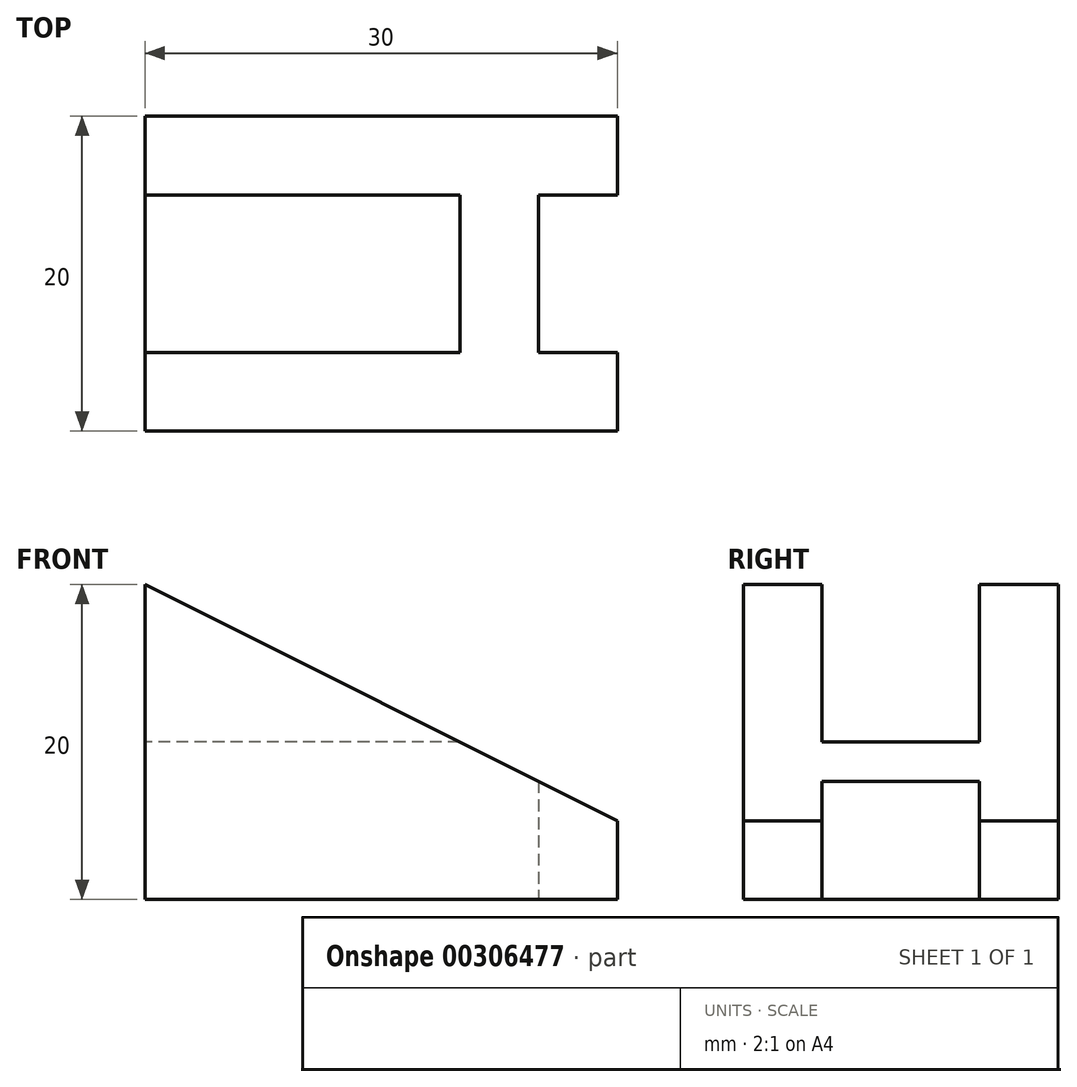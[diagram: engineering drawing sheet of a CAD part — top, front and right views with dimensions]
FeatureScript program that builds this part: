
annotation { "Feature Type Name" : "Feature", "Feature Type Description" : "" }
export const myFeature = defineFeature(function(context is Context, id is Id, definition is map)
    precondition{}
    {
        {
            var Q0;
            Q0=qCreatedBy(makeId("Front.planeOp"),FACE);
            var sketch = newSketch(context, id + "F0", { "sketchPlane" : qUnion([Q0])});
            skLineSegment(sketch, "E0", {"start": v(0, 0) * mm, "end": v(30, 0) * mm});
            skLineSegment(sketch, "E1", {"start": v(30, 0) * mm, "end": v(30, 5) * mm});
            skLineSegment(sketch, "E2", {"start": v(30, 5) * mm, "end": v(0, 20) * mm});
            skLineSegment(sketch, "E3", {"start": v(0, 20) * mm, "end": v(0, 0) * mm});
            skSolve(sketch);
        }
        {
            var Q0;
            Q0=makeQuery(id+"F0.imprint","IMPRINT",FACE,{"disambiguationData":[TD([[makeQuery(id+"F0.imprint","IMPRINT",EDGE,{"derivedFrom":sQuery(id+"F0.wireOp",EDGE,"E0")}),1.0]])]});
            extrude(context, id + "F1", {"entities" : qUnion([Q0]), "depth" : 20 * mm});
        }
        {
            var Q0;
            Q0=makeQuery(id+"F1.opExtrude","SWEPT_FACE",FACE,{"disambiguationData":[OSD([sQuery(id+"F0.wireOp",EDGE,"E0")])]});
            var sketch = newSketch(context, id + "F2", { "sketchPlane" : qUnion([Q0])});
            skLineSegment(sketch, "E4.bottom", {"start": v(30, 15) * mm, "end": v(25, 15) * mm});
            skLineSegment(sketch, "E4.top", {"start": v(30, 5) * mm, "end": v(25, 5) * mm});
            skLineSegment(sketch, "E4.left", {"start": v(30, 15) * mm, "end": v(30, 5) * mm});
            skLineSegment(sketch, "E4.right", {"start": v(25, 15) * mm, "end": v(25, 5) * mm});
            skSolve(sketch);
        }
        {
            var Q0;
            Q0=makeQuery(id+"F2.imprint","IMPRINT",FACE,{"disambiguationData":[TD([[makeQuery(id+"F2.imprint","IMPRINT",EDGE,{"derivedFrom":sQuery(id+"F2.wireOp",EDGE,"E4.bottom")}),1.0]])]});
            extrude(context, id + "F3", {"entities" : qUnion([Q0]), "operationType" : NewBodyOperationType.REMOVE, "oppositeDirection" : true, "depth" : 25 * mm});
        }
        {
            var Q0;
            Q0=makeQuery(id+"F1.opExtrude","SWEPT_FACE",FACE,{"disambiguationData":[OSD([sQuery(id+"F0.wireOp",EDGE,"E3")])]});
            var sketch = newSketch(context, id + "F4", { "sketchPlane" : qUnion([Q0])});
            skLineSegment(sketch, "E5.bottom", {"start": v(5, 20) * mm, "end": v(15, 20) * mm});
            skLineSegment(sketch, "E5.top", {"start": v(5, 10) * mm, "end": v(15, 10) * mm});
            skLineSegment(sketch, "E5.left", {"start": v(5, 20) * mm, "end": v(5, 10) * mm});
            skLineSegment(sketch, "E5.right", {"start": v(15, 20) * mm, "end": v(15, 10) * mm});
            skSolve(sketch);
        }
        {
            var Q0;
            Q0=makeQuery(id+"F4.imprint","IMPRINT",FACE,{"disambiguationData":[TD([[makeQuery(id+"F4.imprint","IMPRINT",EDGE,{"derivedFrom":sQuery(id+"F4.wireOp",EDGE,"E5.bottom")}),1.0]])]});
            extrude(context, id + "F5", {"entities" : qUnion([Q0]), "operationType" : NewBodyOperationType.REMOVE, "oppositeDirection" : true, "depth" : 25 * mm});
        }
    });
